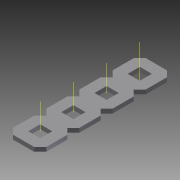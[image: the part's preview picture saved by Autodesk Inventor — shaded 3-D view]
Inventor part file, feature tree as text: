
AUTODESK INVENTOR PART (.ipt)
format: ipt  version: 2015 (Build 190159000, 159)  size: 1,118,208 bytes
history: native  units: in
note: dims shown in document units (in); Inventor stores cm internally (conversion verified against a paired STEP export)
features: other x13, extrude x2, pattern_linear x1, imported_body x1
ambient origin geometry x8: Origin, YZ Plane, XZ Plane, XY Plane, X Axis, Y Axis, Z Axis, Center Point
bodies: Body1 (feature_tree)
feature tree (17):
  other  "Diamond-Pattern"
  other  "Plate"
  extrude  "length cut"  TaperAngle=0.0deg  [1 undecoded]
  extrude  "width cut"  TaperAngle=0.0deg  [1 undecoded]
  other  "constraint axis"
  pattern_linear  "constraint axes"  Spacing1=0.5in  [1 undecoded]
  other  "front plane"
  other  "right plane"
  imported_body  "Base1"
  other  "length profile"
  other  "width profile"
  other  "Work Point1"
  other  "back plane"
  other  "left plane"
  other  "Work Axis170"
  other  "Work Axis171"
  other  "Work Axis172"
note: 3 required parameter values undecoded (feature->parameter linkage not recoverable at this tier; creation-order binding heuristic only, values carry confidence <= 0.55)
